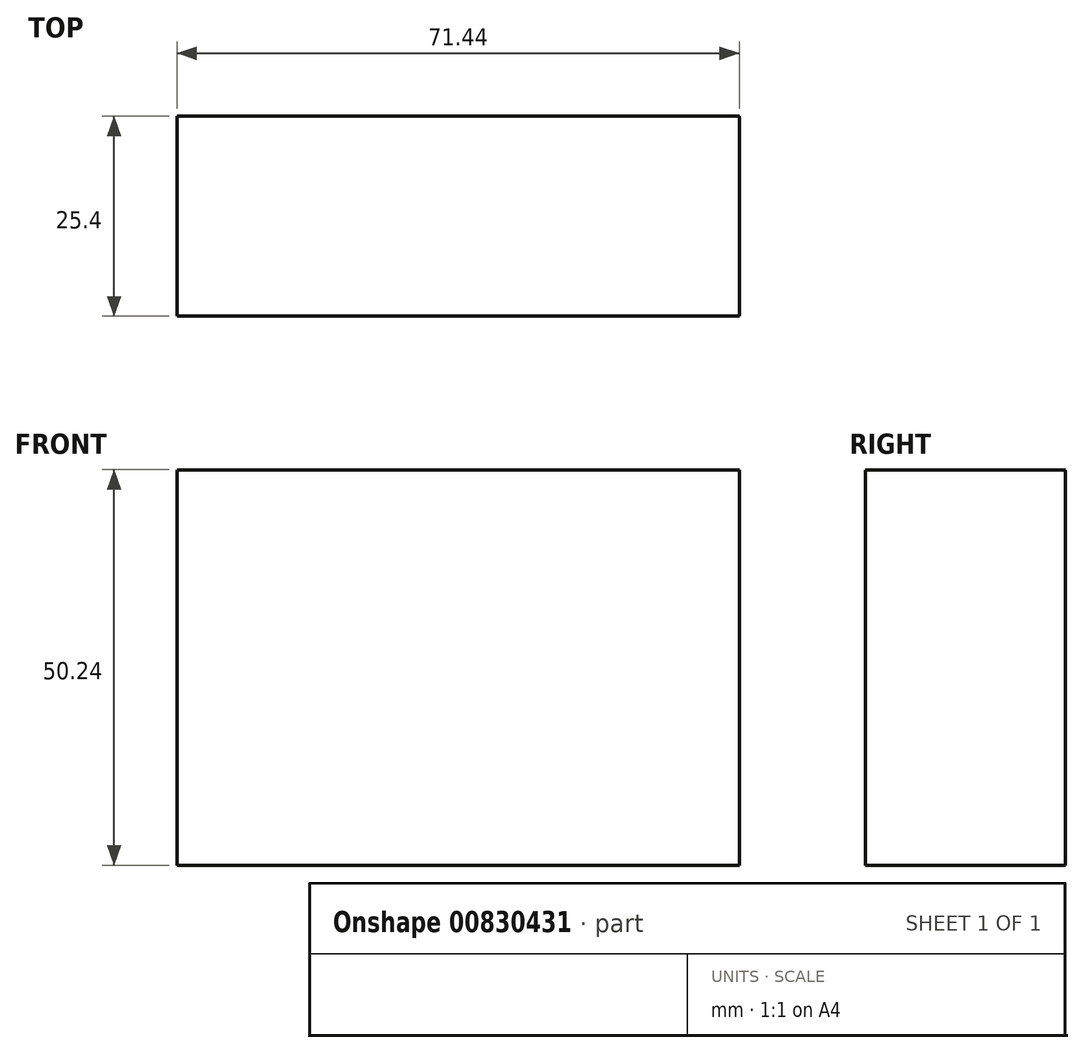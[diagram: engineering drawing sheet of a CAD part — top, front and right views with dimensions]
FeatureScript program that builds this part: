
annotation { "Feature Type Name" : "Feature", "Feature Type Description" : "" }
export const myFeature = defineFeature(function(context is Context, id is Id, definition is map)
    precondition{}
    {
        {
            var Q0;
            Q0=qCreatedBy(makeId("Front.planeOp"),FACE);
            var sketch = newSketch(context, id + "F0", { "sketchPlane" : qUnion([Q0])});
            skLineSegment(sketch, "E0.bottom", {"start": v(0, 0) * mm, "end": v(71.44, 0) * mm});
            skLineSegment(sketch, "E0.top", {"start": v(0, 50.24) * mm, "end": v(71.44, 50.24) * mm});
            skLineSegment(sketch, "E0.left", {"start": v(0, 0) * mm, "end": v(0, 50.24) * mm});
            skLineSegment(sketch, "E0.right", {"start": v(71.44, 0) * mm, "end": v(71.44, 50.24) * mm});
            skSolve(sketch);
        }
        {
            var Q0;
            Q0=makeQuery(id+"F0.imprint","IMPRINT",FACE,{"disambiguationData":[TD([[makeQuery(id+"F0.imprint","IMPRINT",EDGE,{"derivedFrom":sQuery(id+"F0.wireOp",EDGE,"E0.bottom")}),1.0]])]});
            extrude(context, id + "F1", {"entities" : qUnion([Q0]), "depth" : 25.4 * mm, "offsetDistance" : 25.4 * mm});
        }
    });
